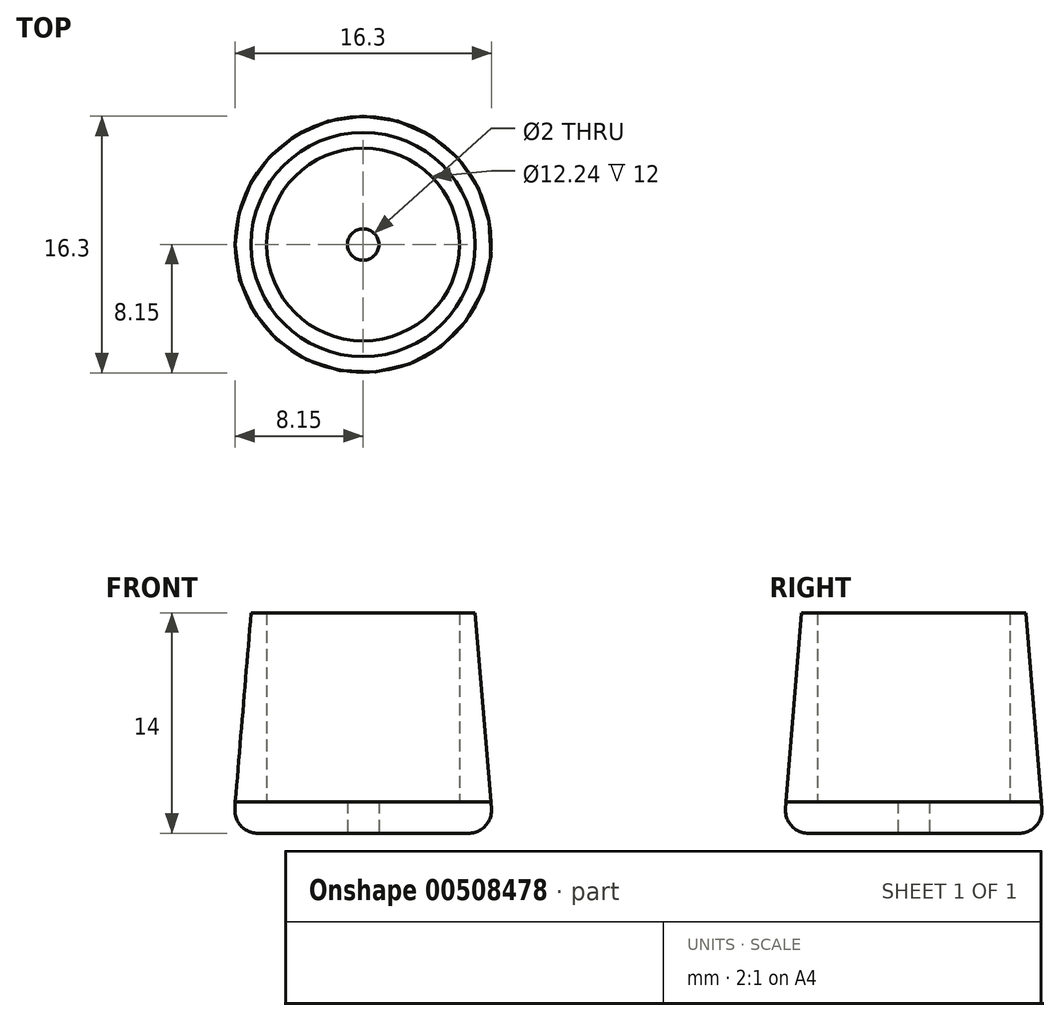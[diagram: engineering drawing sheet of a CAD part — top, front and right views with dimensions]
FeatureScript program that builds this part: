
annotation { "Feature Type Name" : "Feature", "Feature Type Description" : "" }
export const myFeature = defineFeature(function(context is Context, id is Id, definition is map)
    precondition{}
    {
        {
            var Q0;
            Q0=qCreatedBy(makeId("Front.planeOp"),FACE);
            var sketch = newSketch(context, id + "F0", { "sketchPlane" : qUnion([Q0])});
            skPoint(sketch, "E0", {"position": v(6.12, 14) * mm});
            skPoint(sketch, "E1", {"position": v(7.12, 14) * mm});
            skPoint(sketch, "E2", {"position": v(1, 2) * mm});
            skLineSegment(sketch, "E3", {"start": v(1, 0) * mm, "end": v(1, 2) * mm});
            skLineSegment(sketch, "E4", {"start": v(1, 2) * mm, "end": v(6.12, 2) * mm});
            skLineSegment(sketch, "E5", {"start": v(1, 0) * mm, "end": v(6.12, 0) * mm});
            skPoint(sketch, "E6", {"position": v(8.12, 2) * mm});
            skLineSegment(sketch, "E7", {"start": v(8.12, 2) * mm, "end": v(8.14, 1.53) * mm});
            skLineSegment(sketch, "E8", {"start": v(6.12, 0) * mm, "end": v(6.7, 0) * mm});
            skPoint(sketch, "E9.visualSharp", {"position": v(8.22, 0) * mm});
            skArc(sketch, "E9.filletArc", {"start": v(6.7, 0) * mm, "mid": v(7.75, 0.45) * mm, "end": v(8.14, 1.53) * mm});
            skLineSegment(sketch, "E10", {"start": v(6.12, 2) * mm, "end": v(6.12, 14) * mm});
            skLineSegment(sketch, "E11", {"start": v(6.12, 14) * mm, "end": v(7.12, 14) * mm});
            skLineSegment(sketch, "E12", {"start": v(7.12, 14) * mm, "end": v(8.12, 2) * mm});
            skSolve(sketch);
        }
        {
            var Q0;
            Q0=qCreatedBy(makeId("Front.planeOp"),FACE);
            var sketch = newSketch(context, id + "F1", { "sketchPlane" : qUnion([Q0])});
            skLineSegment(sketch, "E13", {"start": v(0, 0) * mm, "end": v(0, 15.02) * mm});
            skSolve(sketch);
        }
        {
            var Q0;
            Q0=makeQuery(id+"F0.imprint","IMPRINT",FACE,{"disambiguationData":[TD([[makeQuery(id+"F0.imprint","IMPRINT",EDGE,{"derivedFrom":sQuery(id+"F0.wireOp",EDGE,"E3")}),-1.0]])]});
            var Q1;
            Q1=sQuery(id+"F1.wireOp",EDGE,"E13");
            revolve(context, id + "F2", {"entities" : qUnion([Q0]), "axis" : qUnion([Q1]), "revolveType" : RevolveType.FULL});
        }
    });
